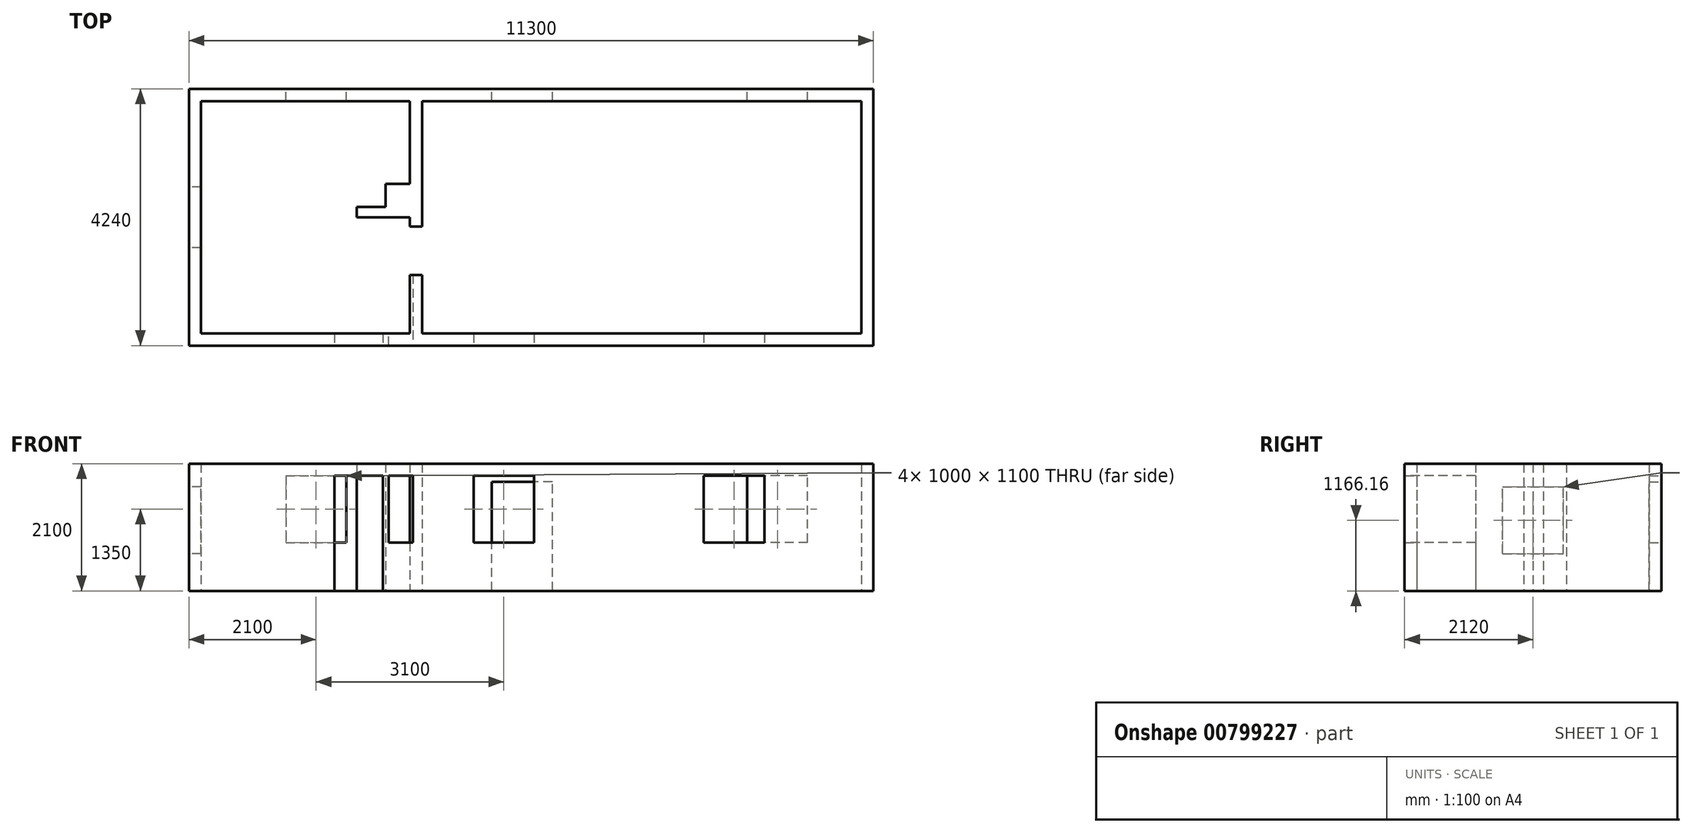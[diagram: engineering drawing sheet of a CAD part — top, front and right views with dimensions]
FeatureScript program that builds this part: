
annotation { "Feature Type Name" : "Feature", "Feature Type Description" : "" }
export const myFeature = defineFeature(function(context is Context, id is Id, definition is map)
    precondition{}
    {
        {
            var Q0;
            Q0=qCreatedBy(makeId("Top.planeOp"),FACE);
            var sketch = newSketch(context, id + "F0", { "sketchPlane" : qUnion([Q0])});
            skLineSegment(sketch, "E0", {"start": v(-5450.86, -2725.57) * mm, "end": v(-2000.86, -2725.57) * mm});
            skLineSegment(sketch, "E1", {"start": v(-2000.86, -2725.57) * mm, "end": v(-2000.86, -1755.57) * mm});
            skLineSegment(sketch, "E2", {"start": v(-2000.86, -1755.57) * mm, "end": v(-1800.86, -1755.57) * mm});
            skLineSegment(sketch, "E3", {"start": v(-1800.86, -1755.57) * mm, "end": v(-1800.86, -2725.57) * mm});
            skLineSegment(sketch, "E4", {"start": v(-1800.86, -2725.57) * mm, "end": v(5449.14, -2725.57) * mm});
            skLineSegment(sketch, "E5", {"start": v(5449.14, -2725.57) * mm, "end": v(5449.14, 1114.43) * mm});
            skLineSegment(sketch, "E6", {"start": v(5449.14, 1114.43) * mm, "end": v(-1800.86, 1114.43) * mm});
            skLineSegment(sketch, "E7", {"start": v(-1800.86, 1114.43) * mm, "end": v(-1800.86, -955.57) * mm});
            skLineSegment(sketch, "E8", {"start": v(-1800.86, -955.57) * mm, "end": v(-2000.86, -955.57) * mm});
            skLineSegment(sketch, "E9", {"start": v(-2000.86, -955.57) * mm, "end": v(-2000.86, -805.57) * mm});
            skLineSegment(sketch, "E10", {"start": v(-2000.86, -805.57) * mm, "end": v(-2880.86, -805.57) * mm});
            skLineSegment(sketch, "E11", {"start": v(-2880.86, -805.57) * mm, "end": v(-2880.86, -635.57) * mm});
            skLineSegment(sketch, "E12", {"start": v(-2880.86, -635.57) * mm, "end": v(-2400.86, -635.57) * mm});
            skLineSegment(sketch, "E13", {"start": v(-2400.86, -635.57) * mm, "end": v(-2400.86, -255.57) * mm});
            skLineSegment(sketch, "E14", {"start": v(-2400.86, -255.57) * mm, "end": v(-2000.86, -255.57) * mm});
            skLineSegment(sketch, "E15", {"start": v(-2000.86, -255.57) * mm, "end": v(-2000.86, 1114.43) * mm});
            skLineSegment(sketch, "E16", {"start": v(-2000.86, 1114.43) * mm, "end": v(-5450.86, 1114.43) * mm});
            skLineSegment(sketch, "E17", {"start": v(-5450.86, 1114.43) * mm, "end": v(-5450.86, -2725.57) * mm});
            skLineSegment(sketch, "E18", {"start": v(-5650.86, 1314.43) * mm, "end": v(-5650.86, -2925.57) * mm});
            skLineSegment(sketch, "E19", {"start": v(-5650.86, -2925.57) * mm, "end": v(5649.14, -2925.57) * mm});
            skLineSegment(sketch, "E20", {"start": v(5649.14, -2925.57) * mm, "end": v(5649.14, 1314.43) * mm});
            skLineSegment(sketch, "E21", {"start": v(5649.14, 1314.43) * mm, "end": v(-5650.86, 1314.43) * mm});
            skSolve(sketch);
        }
        {
            var Q0;
            Q0=makeQuery(id+"F0.imprint","IMPRINT",FACE,{"disambiguationData":[TD([[makeQuery(id+"F0.imprint","IMPRINT",EDGE,{"derivedFrom":sQuery(id+"F0.wireOp",EDGE,"E0")}),-1.0]])]});
            extrude(context, id + "F1", {"entities" : qUnion([Q0]), "depth" : 2100 * mm, "offsetDistance" : 25 * mm});
        }
        {
            var Q0;
            Q0=makeQuery(id+"F1.opExtrude","SWEPT_FACE",FACE,{"disambiguationData":[OSD([sQuery(id+"F0.wireOp",EDGE,"E19")])]});
            var sketch = newSketch(context, id + "F2", { "sketchPlane" : qUnion([Q0])});
            skLineSegment(sketch, "E22.bottom", {"start": v(2849.14, 800) * mm, "end": v(3849.14, 800) * mm});
            skLineSegment(sketch, "E22.top", {"start": v(2849.14, 1900) * mm, "end": v(3849.14, 1900) * mm});
            skLineSegment(sketch, "E22.left", {"start": v(2849.14, 800) * mm, "end": v(2849.14, 1900) * mm});
            skLineSegment(sketch, "E22.right", {"start": v(3849.14, 800) * mm, "end": v(3849.14, 1900) * mm});
            skLineSegment(sketch, "E23.bottom", {"start": v(-950.86, 1900) * mm, "end": v(49.14, 1900) * mm});
            skLineSegment(sketch, "E23.top", {"start": v(-950.86, 800) * mm, "end": v(49.14, 800) * mm});
            skLineSegment(sketch, "E23.left", {"start": v(-950.86, 1900) * mm, "end": v(-950.86, 800) * mm});
            skLineSegment(sketch, "E23.right", {"start": v(49.14, 1900) * mm, "end": v(49.14, 800) * mm});
            skLineSegment(sketch, "E24.bottom", {"start": v(-1950.86, 1900) * mm, "end": v(-2450.86, 1900) * mm});
            skLineSegment(sketch, "E24.top", {"start": v(-1950.86, 800) * mm, "end": v(-2450.86, 800) * mm});
            skLineSegment(sketch, "E24.left", {"start": v(-1950.86, 1900) * mm, "end": v(-1950.86, 800) * mm});
            skLineSegment(sketch, "E24.right", {"start": v(-2450.86, 1900) * mm, "end": v(-2450.86, 800) * mm});
            skLineSegment(sketch, "E25.bottom", {"start": v(-2450.86, 1900) * mm, "end": v(-3250.86, 1900) * mm});
            skLineSegment(sketch, "E25.top", {"start": v(-2450.86, 0) * mm, "end": v(-3250.86, 0) * mm});
            skLineSegment(sketch, "E25.left", {"start": v(-2450.86, 1900) * mm, "end": v(-2450.86, 0) * mm});
            skLineSegment(sketch, "E25.right", {"start": v(-3250.86, 1900) * mm, "end": v(-3250.86, 0) * mm});
            skSolve(sketch);
        }
        {
            var Q0;
            Q0=makeQuery(id+"F1.opExtrude","SWEPT_FACE",FACE,{"disambiguationData":[OSD([sQuery(id+"F0.wireOp",EDGE,"E18")])]});
            var sketch = newSketch(context, id + "F3", { "sketchPlane" : qUnion([Q0])});
            skLineSegment(sketch, "E26.bottom", {"start": v(1305.57, 616.16) * mm, "end": v(305.57, 616.16) * mm});
            skLineSegment(sketch, "E26.top", {"start": v(1305.57, 1716.16) * mm, "end": v(305.57, 1716.16) * mm});
            skLineSegment(sketch, "E26.left", {"start": v(1305.57, 616.16) * mm, "end": v(1305.57, 1716.16) * mm});
            skLineSegment(sketch, "E26.right", {"start": v(305.57, 616.16) * mm, "end": v(305.57, 1716.16) * mm});
            skPoint(sketch, "E26.middle", {"position": v(805.57, 1166.16) * mm});
            skPoint(sketch, "E26.middle.positionSnap0", {"position": v(805.57, 0) * mm});
            skPoint(sketch, "E26.centerSnap0", {"position": v(805.57, 0) * mm});
            skSolve(sketch);
        }
        {
            var Q0;
            Q0=makeQuery(id+"F1.opExtrude","SWEPT_FACE",FACE,{"disambiguationData":[OSD([sQuery(id+"F0.wireOp",EDGE,"E21")])]});
            var sketch = newSketch(context, id + "F4", { "sketchPlane" : qUnion([Q0])});
            skLineSegment(sketch, "E27.bottom", {"start": v(-4564.38, 800) * mm, "end": v(-3564.38, 800) * mm});
            skLineSegment(sketch, "E27.top", {"start": v(-4564.38, 1900) * mm, "end": v(-3564.38, 1900) * mm});
            skLineSegment(sketch, "E27.left", {"start": v(-4564.38, 800) * mm, "end": v(-4564.38, 1900) * mm});
            skLineSegment(sketch, "E27.right", {"start": v(-3564.38, 800) * mm, "end": v(-3564.38, 1900) * mm});
            skLineSegment(sketch, "E28.bottom", {"start": v(-349.14, 0) * mm, "end": v(650.86, 0) * mm});
            skLineSegment(sketch, "E28.top", {"start": v(-349.14, 1800) * mm, "end": v(650.86, 1800) * mm});
            skLineSegment(sketch, "E28.left", {"start": v(-349.14, 0) * mm, "end": v(-349.14, 1800) * mm});
            skLineSegment(sketch, "E28.right", {"start": v(650.86, 0) * mm, "end": v(650.86, 1800) * mm});
            skLineSegment(sketch, "E29.bottom", {"start": v(4050.86, 1900) * mm, "end": v(3050.86, 1900) * mm});
            skLineSegment(sketch, "E29.top", {"start": v(4050.86, 800) * mm, "end": v(3050.86, 800) * mm});
            skLineSegment(sketch, "E29.left", {"start": v(4050.86, 1900) * mm, "end": v(4050.86, 800) * mm});
            skLineSegment(sketch, "E29.right", {"start": v(3050.86, 1900) * mm, "end": v(3050.86, 800) * mm});
            skSolve(sketch);
        }
        {
            var Q0;
            Q0=makeQuery(id+"F2.imprint","IMPRINT",FACE,{"disambiguationData":[TD([[makeQuery(id+"F2.imprint","IMPRINT",EDGE,{"derivedFrom":sQuery(id+"F2.wireOp",EDGE,"E22.bottom")}),1.0]])]});
            var Q1;
            Q1=makeQuery(id+"F2.imprint","IMPRINT",FACE,{"disambiguationData":[TD([[makeQuery(id+"F2.imprint","IMPRINT",EDGE,{"derivedFrom":sQuery(id+"F2.wireOp",EDGE,"E23.bottom")}),-1.0]])]});
            var Q2;
            {var subQ0=sQuery(id+"F2.wireOp",EDGE,"E24.bottom");Q2=makeQuery(id+"F2.imprint","IMPRINT",FACE,{"disambiguationData":[TD([[makeQuery(id+"F2.imprint","IMPRINT",EDGE,{"derivedFrom":subQ0}),1.0]])]});}
            var Q3;
            {var subQ3=sQuery(id+"F2.wireOp",EDGE,"E25.bottom");Q3=makeQuery(id+"F2.imprint","IMPRINT",FACE,{"disambiguationData":[TD([[makeQuery(id+"F2.imprint","IMPRINT",EDGE,{"derivedFrom":subQ3}),1.0]])]});}
            extrude(context, id + "F5", {"entities" : qUnion([Q0, Q1, Q2, Q3]), "operationType" : NewBodyOperationType.REMOVE, "endBound" : BoundingType.UP_TO_NEXT, "oppositeDirection" : true, "depth" : 300 * mm, "offsetDistance" : 25 * mm});
        }
        {
            var Q0;
            Q0=makeQuery(id+"F3.imprint","IMPRINT",FACE,{"disambiguationData":[TD([[makeQuery(id+"F3.imprint","IMPRINT",EDGE,{"derivedFrom":sQuery(id+"F3.wireOp",EDGE,"E26.bottom")}),-1.0]])]});
            extrude(context, id + "F6", {"entities" : qUnion([Q0]), "operationType" : NewBodyOperationType.REMOVE, "endBound" : BoundingType.UP_TO_NEXT, "oppositeDirection" : true, "depth" : 25 * mm, "offsetDistance" : 25 * mm});
        }
        {
            var Q0;
            Q0=makeQuery(id+"F4.imprint","IMPRINT",FACE,{"disambiguationData":[TD([[makeQuery(id+"F4.imprint","IMPRINT",EDGE,{"derivedFrom":sQuery(id+"F4.wireOp",EDGE,"E27.bottom")}),1.0]])]});
            var Q1;
            Q1=makeQuery(id+"F4.imprint","IMPRINT",FACE,{"disambiguationData":[TD([[makeQuery(id+"F4.imprint","IMPRINT",EDGE,{"derivedFrom":sQuery(id+"F4.wireOp",EDGE,"E28.bottom")}),1.0]])]});
            var Q2;
            Q2=makeQuery(id+"F4.imprint","IMPRINT",FACE,{"disambiguationData":[TD([[makeQuery(id+"F4.imprint","IMPRINT",EDGE,{"derivedFrom":sQuery(id+"F4.wireOp",EDGE,"E29.bottom")}),1.0]])]});
            extrude(context, id + "F7", {"entities" : qUnion([Q0, Q1, Q2]), "operationType" : NewBodyOperationType.REMOVE, "endBound" : BoundingType.UP_TO_NEXT, "oppositeDirection" : true, "depth" : 25 * mm, "offsetDistance" : 25 * mm});
        }
        {
            var Q0;
            Q0=makeQuery(id+"F5.boolean.opBoolean","COPY",FACE,{"derivedFrom":makeQuery(id+"F5.opExtrude","SWEPT_FACE",FACE,{"disambiguationData":[OSD([sQuery(id+"F2.wireOp",EDGE,"E24.top")])]})});
            var sketch = newSketch(context, id + "F8", { "sketchPlane" : qUnion([Q0])});
            skLineSegment(sketch, "E30.bottom", {"start": v(-2450.86, -2925.57) * mm, "end": v(-2350.86, -2925.57) * mm});
            skLineSegment(sketch, "E30.top", {"start": v(-2450.86, -2725.57) * mm, "end": v(-2350.86, -2725.57) * mm});
            skLineSegment(sketch, "E30.left", {"start": v(-2450.86, -2925.57) * mm, "end": v(-2450.86, -2725.57) * mm});
            skLineSegment(sketch, "E30.right", {"start": v(-2350.86, -2925.57) * mm, "end": v(-2350.86, -2725.57) * mm});
            skSolve(sketch);
        }
        {
            var Q0;
            Q0=makeQuery(id+"F8.imprint","IMPRINT",FACE,{"disambiguationData":[TD([[makeQuery(id+"F8.imprint","IMPRINT",EDGE,{"derivedFrom":sQuery(id+"F8.wireOp",EDGE,"E30.bottom")}),-1.0]])]});
            extrude(context, id + "F9", {"entities" : qUnion([Q0]), "operationType" : NewBodyOperationType.ADD, "endBound" : BoundingType.UP_TO_NEXT, "depth" : 25 * mm, "offsetDistance" : 25 * mm});
        }
    });
